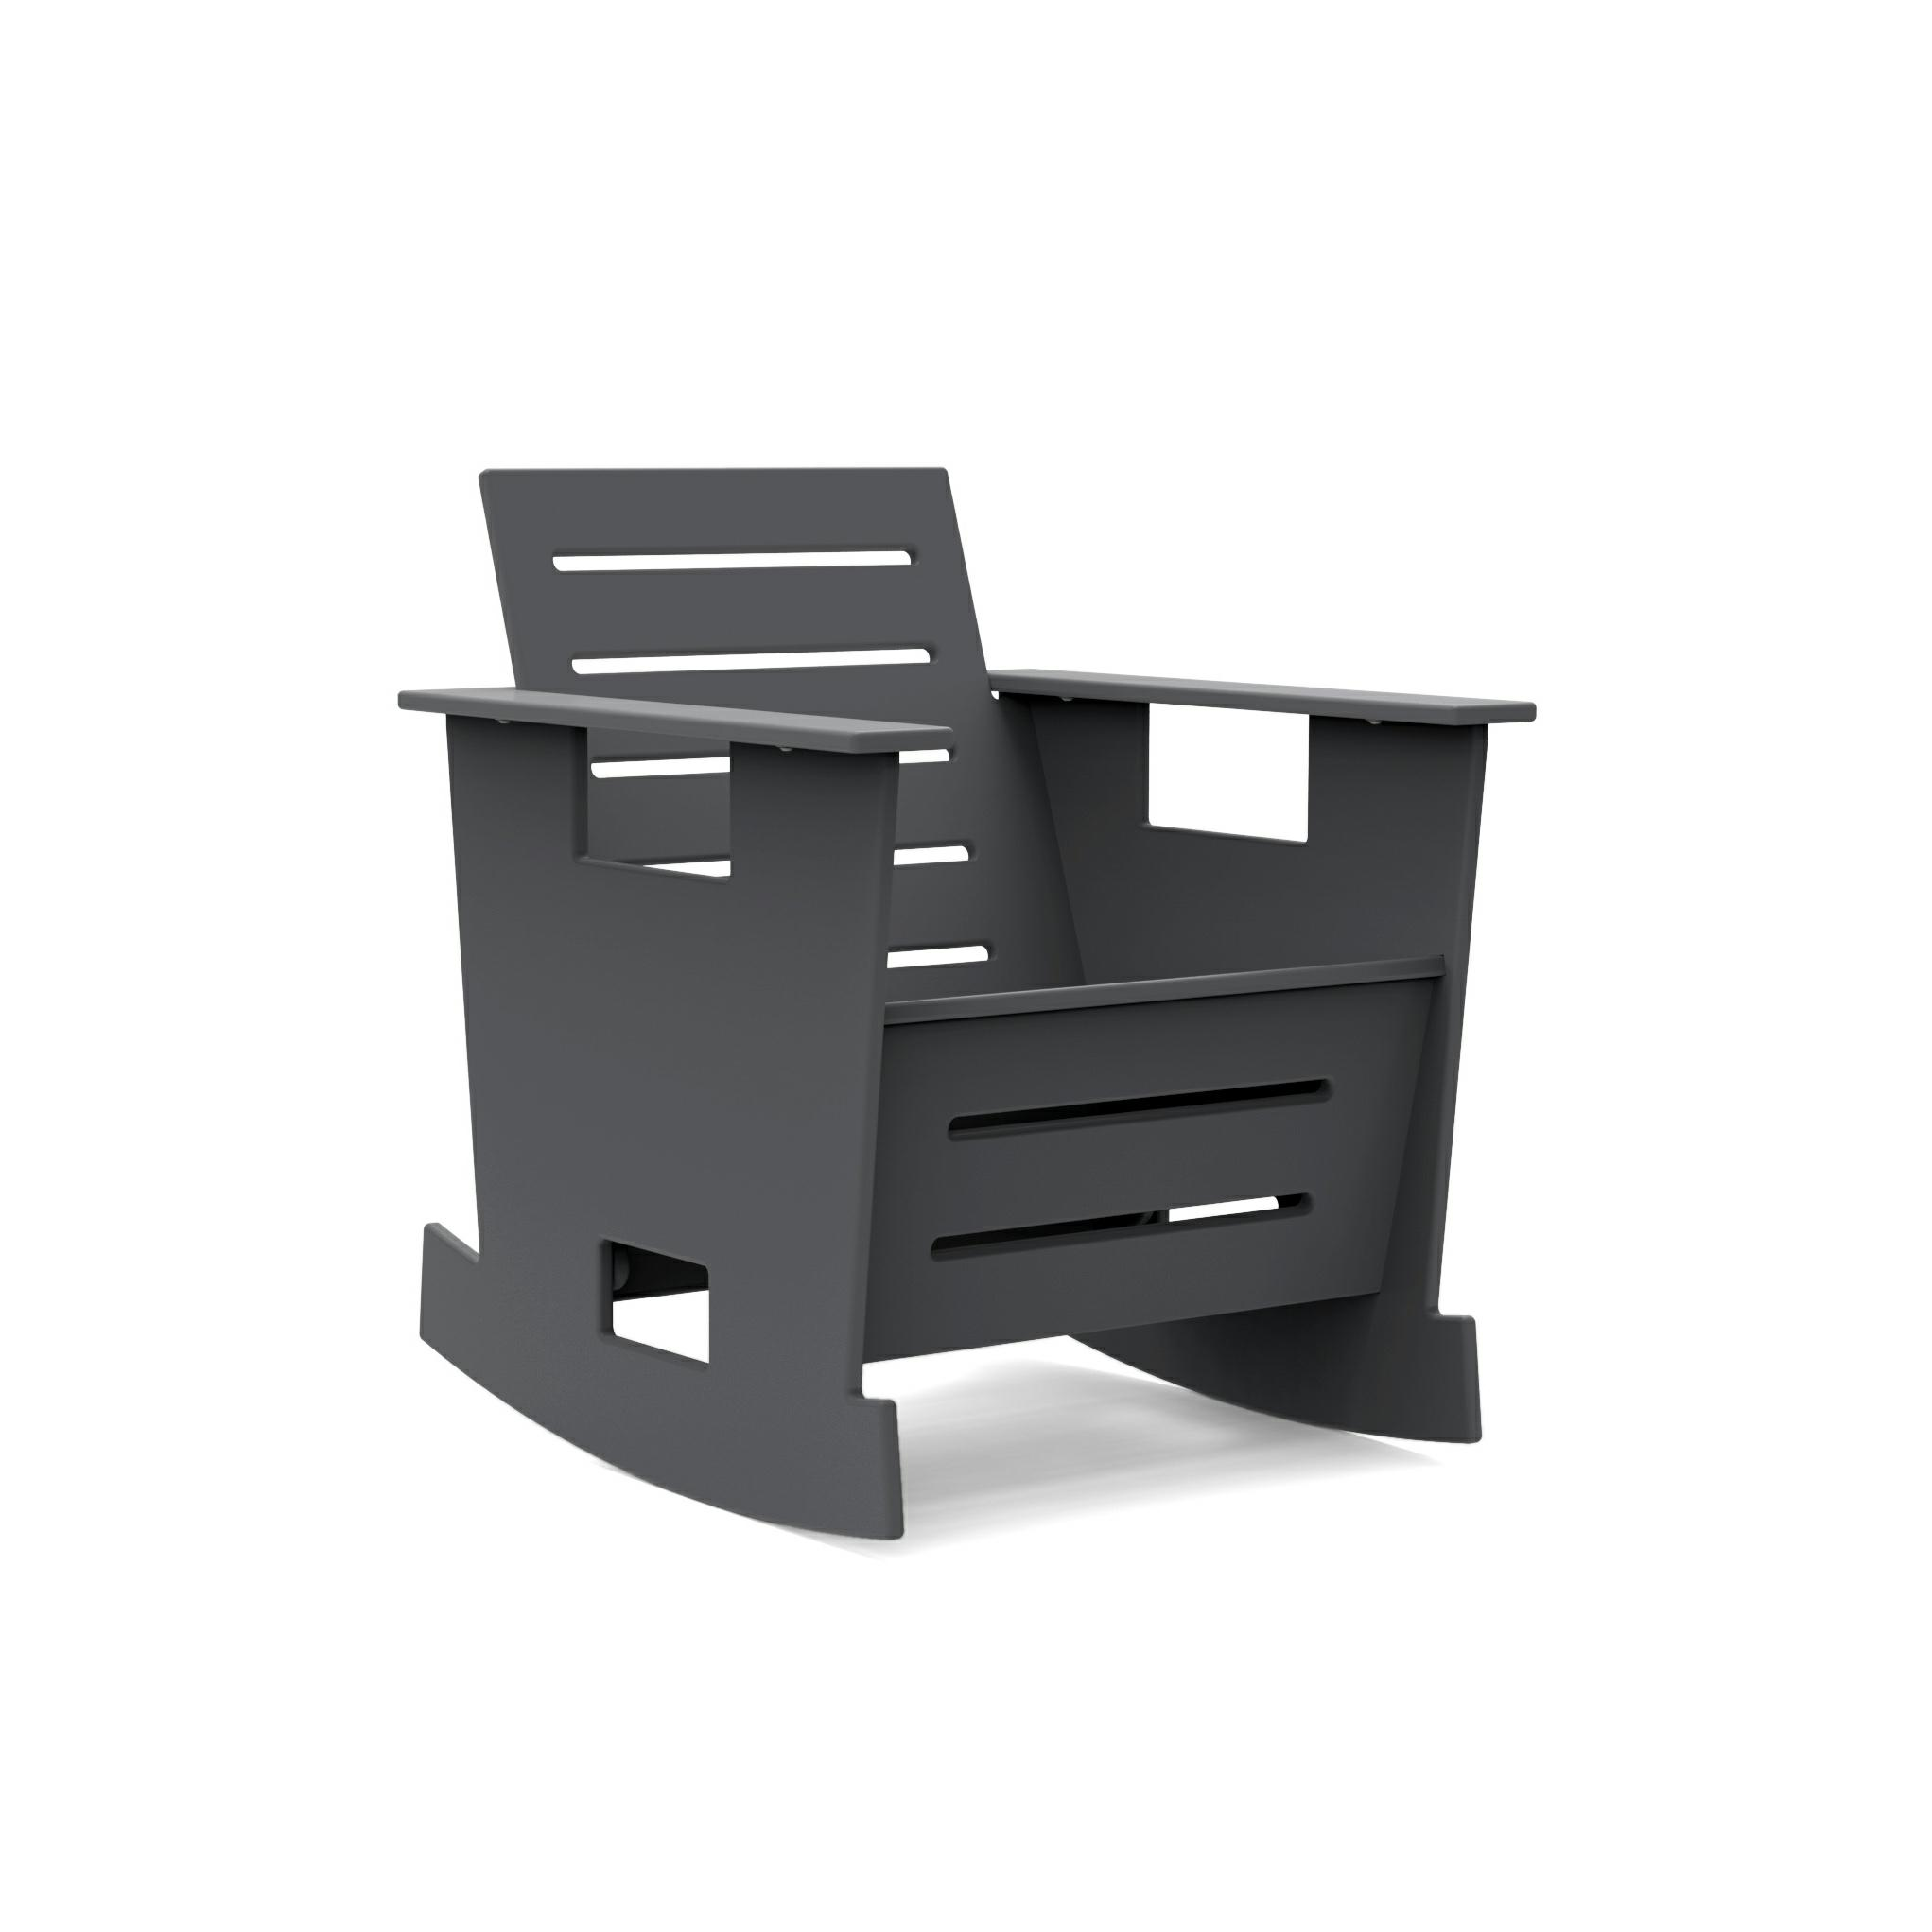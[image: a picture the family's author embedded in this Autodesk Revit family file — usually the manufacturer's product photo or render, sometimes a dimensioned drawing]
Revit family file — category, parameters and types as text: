
# Revit family: Lollygagger Go Club Rocker
name_source: partatom
category: Furniture
revit_build: Autodesk Revit 2016 (Build: 20150220_1215(x64)
units: mm (PartAtom-declared; Revit-internal decimal feet)

## family parameters
Always vertical = Yes
Cut with Voids When Loaded = No
OmniClass Number = 23.40.20.00
OmniClass Title = General Furniture and Specialties
Room Calculation Point = No
Shared = No
Work Plane-Based = No

## types (11) — shared parameters
Apron = 1' - 3 3/4"
Height Top = 2' - 0"
Length = 2' - 2 5/8"
Manufacturer = Loll
Thick = 0' - 1"
Type Image = go_club rocker.jpg
URL = https://lolldesigns.com
Width = 2' - 2"

## type names (no varying parameters)
- Loll-Black
- Loll-Sunset
- Loll-Chocolate
- Loll-Sky
- Loll-Apple
- Loll-Leaf
- Loll-Evergreen
- Loll-Charcoal
- Loll-Sand
- Loll-Navy Blue
- Loll-White

note: column(s) folded — value = type name in every type: Finish Material

## geometry (parser evidence)
native form markers: Sweep x2
no freeform markers — native parametric forms only
